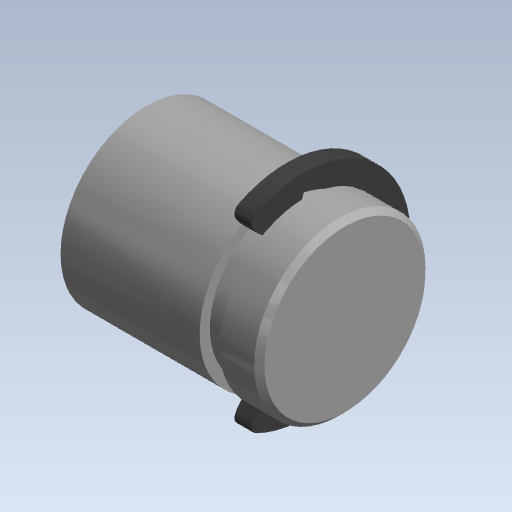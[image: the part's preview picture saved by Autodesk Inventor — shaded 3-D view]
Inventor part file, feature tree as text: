
AUTODESK INVENTOR PART (.ipt)
format: ipt  version: 2020 (Build 240168000, 168)  size: 107,008 bytes
history: native  units: mm (DEFAULTED — no unit token found)
features: extrude x1, revolve x1
ambient origin geometry x8: Origin, YZ Plane, XZ Plane, XY Plane, X Axis, Y Axis, Z Axis, Center Point
bodies: Solid1 (feature_tree), Solid2 (feature_tree)
feature tree (2):
  extrude  "Extrude1"  [1 undecoded]
  revolve  "Revolve1"  [1 undecoded]
note: 2 required parameter values undecoded (feature->parameter linkage not recoverable at this tier; creation-order binding heuristic only, values carry confidence <= 0.55)
